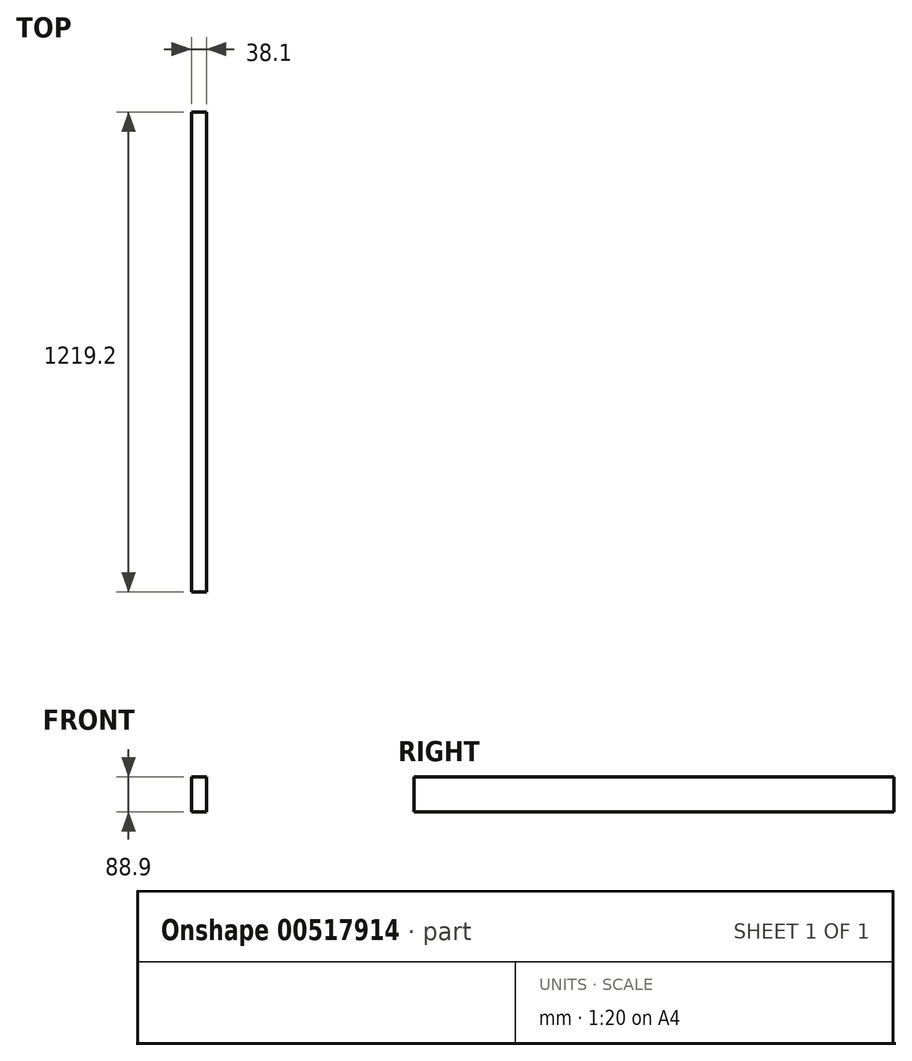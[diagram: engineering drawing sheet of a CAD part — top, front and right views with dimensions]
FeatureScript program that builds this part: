
annotation { "Feature Type Name" : "Feature", "Feature Type Description" : "" }
export const myFeature = defineFeature(function(context is Context, id is Id, definition is map)
    precondition{}
    {
        {
            var Q0;
            Q0=qCreatedBy(makeId("Front.planeOp"),FACE);
            var sketch = newSketch(context, id + "F0", { "sketchPlane" : qUnion([Q0])});
            skLineSegment(sketch, "E0.bottom", {"start": v(19.05, 44.45) * mm, "end": v(-19.05, 44.45) * mm});
            skLineSegment(sketch, "E0.top", {"start": v(19.05, -44.45) * mm, "end": v(-19.05, -44.45) * mm});
            skLineSegment(sketch, "E0.left", {"start": v(19.05, 44.45) * mm, "end": v(19.05, -44.45) * mm});
            skLineSegment(sketch, "E0.right", {"start": v(-19.05, 44.45) * mm, "end": v(-19.05, -44.45) * mm});
            skPoint(sketch, "E0.middle", {"position": v(0, 0) * mm});
            skSolve(sketch);
        }
        {
            var Q0;
            Q0=makeQuery(id+"F0.imprint","IMPRINT",FACE,{"disambiguationData":[TD([[makeQuery(id+"F0.imprint","IMPRINT",EDGE,{"derivedFrom":sQuery(id+"F0.wireOp",EDGE,"E0.bottom")}),1.0]])]});
            extrude(context, id + "F1", {"entities" : qUnion([Q0]), "endBound" : BoundingType.SYMMETRIC, "depth" : 1219.2 * mm, "offsetDistance" : 25.4 * mm});
        }
    });
